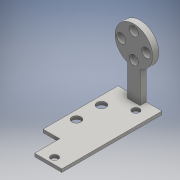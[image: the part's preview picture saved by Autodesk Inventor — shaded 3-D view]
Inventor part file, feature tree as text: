
AUTODESK INVENTOR PART (.ipt)
format: ipt  version: 2016 (Build 200138000, 138)  size: 190,976 bytes
history: native  units: mm
features: sketch x6, extrude x4, hole x2
ambient origin geometry x8: Origin, YZ Plane, XZ Plane, XY Plane, X Axis, Y Axis, Z Axis, Center Point
bodies: Solid1 (feature_tree)
feature tree (12):
  extrude  "Extrusion1"  Depth=4.35mm
  extrude  "Extrusion2"  Depth=6.0mm
  extrude  "Extrusion3"  Depth=6.0mm
  hole  "Hole1"  [1 undecoded]
  hole  "Hole2"  [1 undecoded]
  extrude  "Extrusion4"  Depth=6.0mm
  sketch  "Sketch1"  dims[d0=18.0mm d1=4.35mm]
  sketch  "Sketch2"  dims[d2=6.0mm d3=4.35mm]
  sketch  "Sketch3"  dims[d4=6.0mm d5=4.35mm]
  sketch  "Sketch4"  dims[d6=6.0mm d7=4.35mm]
  sketch  "Sketch5"  dims[d8=6.0mm d9=3.0mm d10=0.0mm]
  sketch  "Sketch6"  dims[d13=6.0mm d14=6.0mm d15=1.5mm d16=48.0mm d17=0.0mm d18=3.5mm d19=3.5mm d21=1.5mm d22=0.0mm d23=3.5mm d24=3.0mm d26=3.5mm d28=3.0mm d29=3.5mm d30=6.0mm d31=4.0mm d32=2.0mm d33=90.0deg d34=8.0mm d35=20.594885mm d36=3.0mm d43=4.0mm d44=4.0mm d45=6.5mm d46=6.5mm d47=12.0mm d48=4.35mm d49=6.0mm d50=4.0mm d51=4.35mm d52=6.0mm d53=4.0mm d54=4.35mm d55=6.0mm d56=4.0mm d57=2.0mm d58=90.0deg d59=8.0mm d60=20.594885mm d61=13.0mm d64=3.0mm d65=0.0mm d66=15.0mm]
note: 2 required parameter values undecoded (feature->parameter linkage not recoverable at this tier; creation-order binding heuristic only, values carry confidence <= 0.55)
